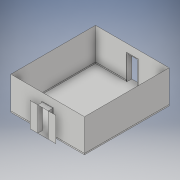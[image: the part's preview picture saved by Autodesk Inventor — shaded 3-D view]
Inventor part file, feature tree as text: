
AUTODESK INVENTOR PART (.ipt)
format: ipt  version: 2017 (Build 210142000, 142)  size: 241,152 bytes
history: native  units: in
note: dims shown in document units (in); Inventor stores cm internally (conversion verified against a paired STEP export)
features: extrude x6, mirror x4, sketch x4, shell x1, other x1
ambient origin geometry x8: Origin, YZ Plane, XZ Plane, XY Plane, X Axis, Y Axis, Z Axis, Center Point
bodies: Solid1 (feature_tree), Solid2 (feature_tree)
feature tree (16):
  extrude  "main body"  Depth=22.0in
  shell  "hollow interior"  Thickness=11.0in
  extrude  "door frame"  Depth=1.0in
  extrude  "Extrusion5"  Depth=2.875in
  extrude  "door trim"  Depth=0.0417in
  extrude  "top of door trim"  Depth=0.1667in
  mirror  "mirror plane for door trim"
  mirror  "Mirror door trim"
  mirror  "mirror plane for door"
  mirror  "Mirror2"
  extrude  "floor trim"  Depth=1.0in TaperAngle=0.0deg
  other  "remove outer edges"
  sketch  "Sketch1"  dims[d0=25.0in d1=22.0in d2=11.0in d3=0.0in]
  sketch  "Sketch3"  dims[d4=1.0in d5=1.4375in]
  sketch  "Sketch4"  dims[d6=6.6667in d7=2.875in]
  sketch  "Sketch5"  dims[d8=1.0in d9=0.0in d10=0.0417in d11=0.1667in d12=1.0in d13=0.0in d14=0.1667in d15=1.0in d16=0.0in d17=7.0in d18=6.6667in d19=0.5in d20=0.0in d21=0.0104in d22=0.0104in d23=0.3438in d24=0.0in d25=0.0104in d26=0.0104in]
